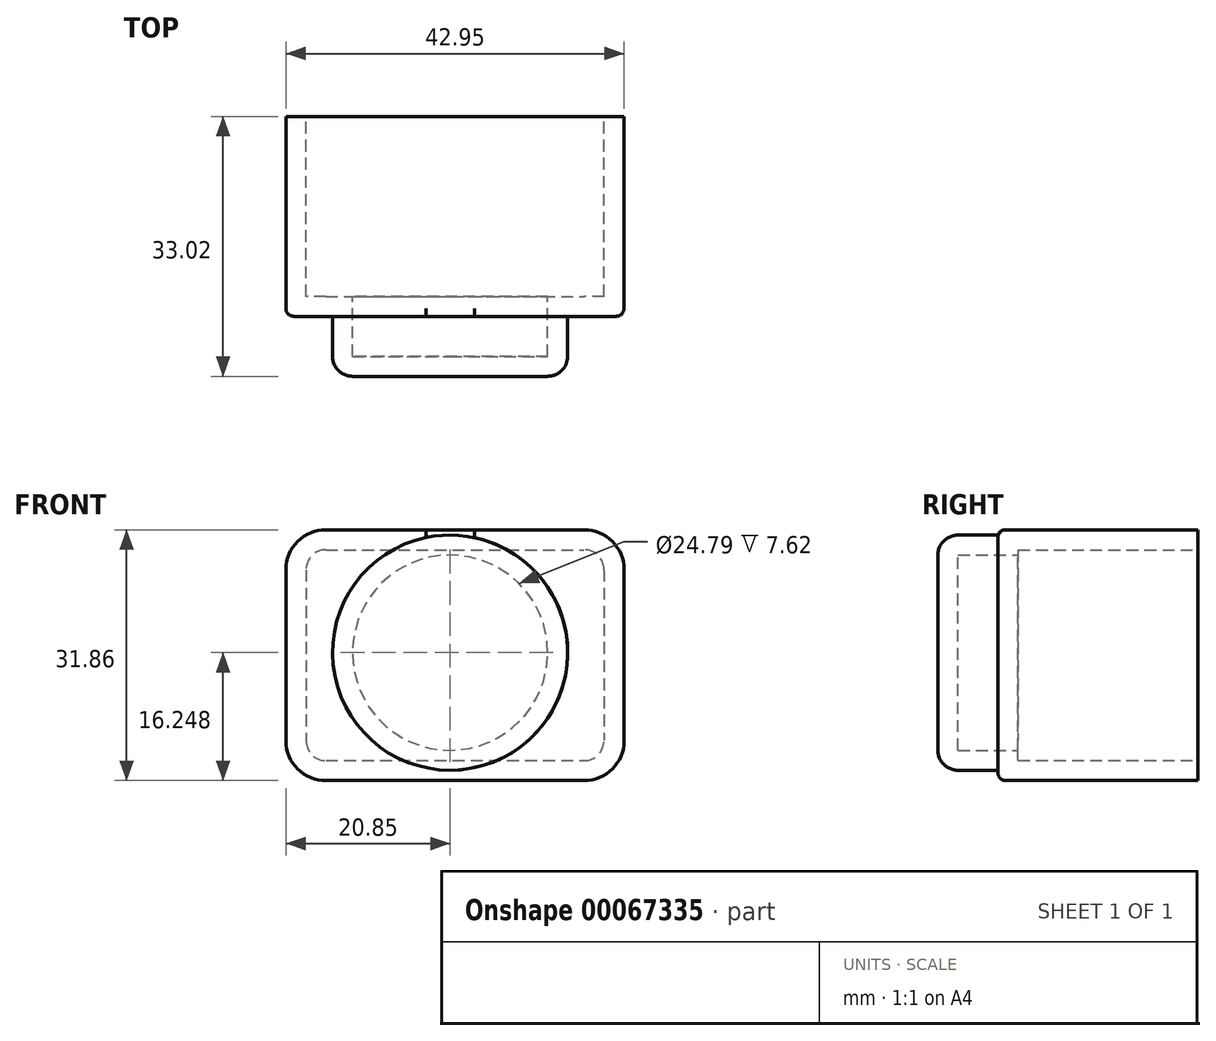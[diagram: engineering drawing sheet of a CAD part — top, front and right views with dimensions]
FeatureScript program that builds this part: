
annotation { "Feature Type Name" : "Feature", "Feature Type Description" : "" }
export const myFeature = defineFeature(function(context is Context, id is Id, definition is map)
    precondition{}
    {
        {
            var Q0;
            Q0=qCreatedBy(makeId("Front.planeOp"),FACE);
            var sketch = newSketch(context, id + "F0", { "sketchPlane" : qUnion([Q0])});
            skLineSegment(sketch, "E0.bottom", {"start": v(-63.5, 49.76) * mm, "end": v(-20.55, 49.76) * mm});
            skLineSegment(sketch, "E0.top", {"start": v(-63.5, 17.9) * mm, "end": v(-20.55, 17.9) * mm});
            skLineSegment(sketch, "E0.left", {"start": v(-63.5, 49.76) * mm, "end": v(-63.5, 17.9) * mm});
            skLineSegment(sketch, "E0.right", {"start": v(-20.55, 49.76) * mm, "end": v(-20.55, 17.9) * mm});
            skSolve(sketch);
        }
        {
            var Q0;
            Q0=makeQuery(id+"F0.imprint","IMPRINT",FACE,{"disambiguationData":[TD([[makeQuery(id+"F0.imprint","IMPRINT",EDGE,{"derivedFrom":sQuery(id+"F0.wireOp",EDGE,"E0.bottom")}),-1.0]])]});
            extrude(context, id + "F1", {"entities" : qUnion([Q0]), "depth" : 25.4 * mm});
        }
        {
            var Q0;
            Q0=makeQuery(id+"F1.opExtrude","SWEPT_EDGE",EDGE,{"disambiguationData":[OSD([sQuery(id+"F0.wireOp",EDGE,"E0.bottom"),sQuery(id+"F0.wireOp",EDGE,"E0.left")])]});
            var Q1;
            Q1=makeQuery(id+"F1.opExtrude","SWEPT_EDGE",EDGE,{"disambiguationData":[OSD([sQuery(id+"F0.wireOp",EDGE,"E0.bottom"),sQuery(id+"F0.wireOp",EDGE,"E0.right")])]});
            var Q2;
            Q2=makeQuery(id+"F1.opExtrude","SWEPT_EDGE",EDGE,{"disambiguationData":[OSD([sQuery(id+"F0.wireOp",EDGE,"E0.top"),sQuery(id+"F0.wireOp",EDGE,"E0.right")])]});
            var Q3;
            Q3=makeQuery(id+"F1.opExtrude","SWEPT_EDGE",EDGE,{"disambiguationData":[OSD([sQuery(id+"F0.wireOp",EDGE,"E0.top"),sQuery(id+"F0.wireOp",EDGE,"E0.left")])]});
            fillet(context, id + "F2", {"entities" : qUnion([Q0, Q1, Q2, Q3]), "radius" : 5.08 * mm, "tangentPropagation" : true, "allowEdgeOverflow" : false});
        }
        {
            var Q0;
            Q0=makeQuery(id+"F1.opExtrude","CAP_FACE",FACE,{"disambiguationData":[OSD([sQuery(id+"F0.wireOp",EDGE,"E0.bottom"),sQuery(id+"F0.wireOp",EDGE,"E0.top"),sQuery(id+"F0.wireOp",EDGE,"E0.left"),sQuery(id+"F0.wireOp",EDGE,"E0.right")])],"isStart":true});
            shell(context, id + "F3", {"entities" : qUnion([Q0]), "thickness" : 2.54 * mm});
        }
        {
            var Q0;
            Q0=makeQuery(id+"F1.opExtrude","CAP_FACE",FACE,{"disambiguationData":[OSD([sQuery(id+"F0.wireOp",EDGE,"E0.bottom"),sQuery(id+"F0.wireOp",EDGE,"E0.top"),sQuery(id+"F0.wireOp",EDGE,"E0.left"),sQuery(id+"F0.wireOp",EDGE,"E0.right")])],"isStart":false});
            var sketch = newSketch(context, id + "F4", { "sketchPlane" : qUnion([Q0])});
            skCircle(sketch, "E1", {"center": v(-42.65, 34.15) * mm, "radius": 14.93 * mm});
            skSolve(sketch);
        }
        {
            var Q0;
            Q0=makeQuery(id+"F4.imprint","IMPRINT",FACE,{"disambiguationData":[TD([[makeQuery(id+"F4.imprint","IMPRINT",EDGE,{"derivedFrom":sQuery(id+"F4.wireOp",EDGE,"E1")}),1.0]])]});
            extrude(context, id + "F5", {"entities" : qUnion([Q0]), "operationType" : NewBodyOperationType.ADD, "depth" : 7.62 * mm});
        }
        {
            var Q0;
            Q0=makeQuery(id+"F5.opExtrude","CAP_EDGE",EDGE,{"disambiguationData":[OSD([sQuery(id+"F4.wireOp",EDGE,"E1")])],"isStart":false});
            fillet(context, id + "F6", {"entities" : qUnion([Q0]), "radius" : 2.54 * mm, "tangentPropagation" : true, "allowEdgeOverflow" : false});
        }
        {
            var Q0;
            Q0=makeQuery(id+"F3.opShell","OFFSET_FACE",FACE,{"disambiguationData":[OSD([sQuery(id+"F0.wireOp",EDGE,"E0.bottom"),sQuery(id+"F0.wireOp",EDGE,"E0.top"),sQuery(id+"F0.wireOp",EDGE,"E0.left"),sQuery(id+"F0.wireOp",EDGE,"E0.right")])]});
            shell(context, id + "F7", {"entities" : qUnion([Q0]), "thickness" : 2.54 * mm});
        }
        {
            var Q0;
            Q0=makeQuery(id+"F1.opExtrude","CAP_EDGE",EDGE,{"disambiguationData":[OSD([sQuery(id+"F0.wireOp",EDGE,"E0.bottom")])],"isStart":false});
            fillet(context, id + "F8", {"entities" : qUnion([Q0]), "radius" : 1 * mm, "tangentPropagation" : true, "allowEdgeOverflow" : false});
        }
    });
